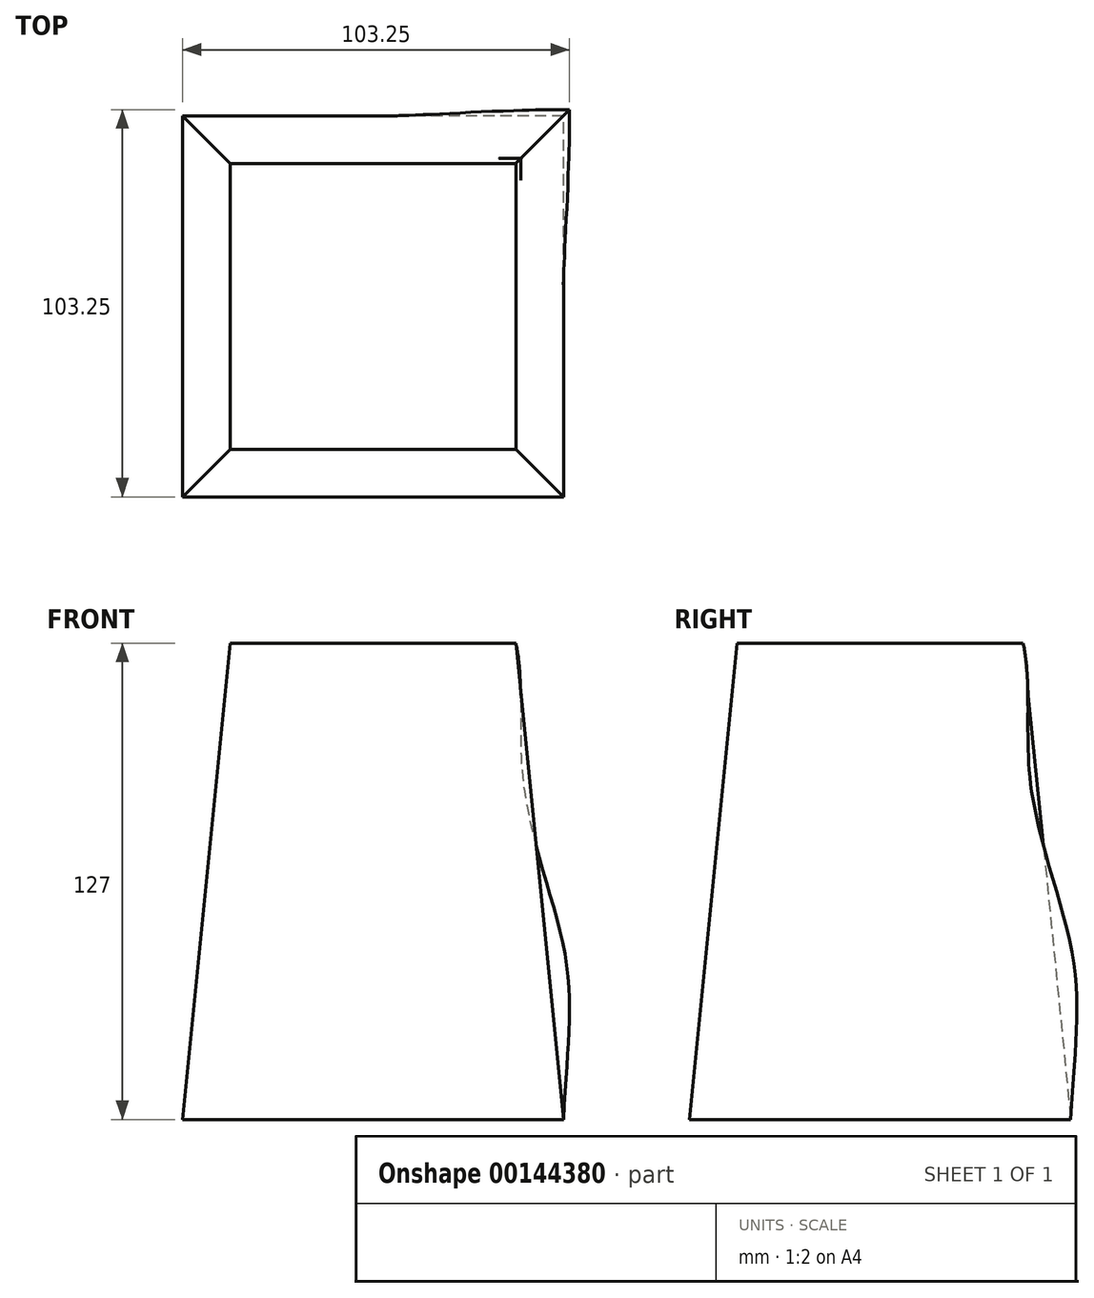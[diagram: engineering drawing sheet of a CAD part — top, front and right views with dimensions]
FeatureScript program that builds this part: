
annotation { "Feature Type Name" : "Feature", "Feature Type Description" : "" }
export const myFeature = defineFeature(function(context is Context, id is Id, definition is map)
    precondition{}
    {
        {
            var Q0;
            Q0=qCreatedBy(makeId("Top.planeOp"),FACE);
            var sketch = newSketch(context, id + "F0", { "sketchPlane" : qUnion([Q0])});
            skLineSegment(sketch, "E0.bottom", {"start": v(50.8, -50.8) * mm, "end": v(-50.8, -50.8) * mm});
            skLineSegment(sketch, "E0.top", {"start": v(50.8, 50.8) * mm, "end": v(-50.8, 50.8) * mm});
            skLineSegment(sketch, "E0.left", {"start": v(50.8, -50.8) * mm, "end": v(50.8, 50.8) * mm});
            skLineSegment(sketch, "E0.right", {"start": v(-50.8, -50.8) * mm, "end": v(-50.8, 50.8) * mm});
            skPoint(sketch, "E0.middle", {"position": v(0, 0) * mm});
            skSolve(sketch);
        }
        {
            var Q0;
            Q0=qCreatedBy(makeId("Top.planeOp"),FACE);
            cPlane(context, id + "F1", {"entities" : qUnion([Q0]), "cplaneType" : CPlaneType.OFFSET, "offset" : 127 * mm, "width" : 152.4 * mm, "height" : 152.4 * mm});
        }
        {
            var Q0;
            Q0=qCreatedBy(id+"F1.planeOp",FACE);
            var sketch = newSketch(context, id + "F2", { "sketchPlane" : qUnion([Q0])});
            skLineSegment(sketch, "E1.bottom", {"start": v(38.1, 38.1) * mm, "end": v(-38.1, 38.1) * mm});
            skLineSegment(sketch, "E1.top", {"start": v(38.1, -38.1) * mm, "end": v(-38.1, -38.1) * mm});
            skLineSegment(sketch, "E1.left", {"start": v(38.1, 38.1) * mm, "end": v(38.1, -38.1) * mm});
            skLineSegment(sketch, "E1.right", {"start": v(-38.1, 38.1) * mm, "end": v(-38.1, -38.1) * mm});
            skPoint(sketch, "E1.middle", {"position": v(0, 0) * mm});
            skSolve(sketch);
        }
        {
            var Q0;
            Q0=sQuery(id+"F2.wireOp",VERTEX,"E1.bottom.start");
            var Q1;
            Q1=sQuery(id+"F2.wireOp",VERTEX,"E1.right.end");
            var Q2;
            Q2=sQuery(id+"F0.wireOp",VERTEX,"E0.right.start");
            cPlane(context, id + "F3", {"entities" : qUnion([Q0, Q1, Q2]), "cplaneType" : CPlaneType.THREE_POINT, "offset" : 25.4 * mm, "width" : 152.4 * mm, "height" : 152.4 * mm});
        }
        {
            var Q0;
            Q0=qCreatedBy(id+"F3.planeOp",FACE);
            var sketch = newSketch(context, id + "F4", { "sketchPlane" : qUnion([Q0])});
            skFitSpline(sketch, "E2", {"points": [v(-53.88, 127) * mm, v(-56.82, 89.06) * mm, v(-72.9, 41.99) * mm, v(-71.84, 0) * mm], "startDerivative": vector(-32.58, -103.67) * mm, "endDerivative": vector(10.34, -156.62) * mm});
            skSolve(sketch);
        }
        {
            var Q0;
            Q0=qCreatedBy(makeId("Front.planeOp"),FACE);
            var sketch = newSketch(context, id + "F5", { "sketchPlane" : qUnion([Q0])});
            skLineSegment(sketch, "E3", {"start": v(0, 0) * mm, "end": v(0, 85.5) * mm});
            skSolve(sketch);
        }
        {
            var Q0;
            Q0=makeQuery(id+"F2.imprint","IMPRINT",FACE,{"disambiguationData":[TD([[makeQuery(id+"F2.imprint","IMPRINT",EDGE,{"derivedFrom":sQuery(id+"F2.wireOp",EDGE,"E1.bottom")}),1.0]])]});
            var Q1;
            Q1=makeQuery(id+"F0.imprint","IMPRINT",FACE,{"disambiguationData":[TD([[makeQuery(id+"F0.imprint","IMPRINT",EDGE,{"derivedFrom":sQuery(id+"F0.wireOp",EDGE,"E0.bottom")}),-1.0]])]});
            var Q2;
            Q2=sQuery(id+"F4.wireOp",EDGE,"E2");
            var Q3;
            Q3=sQuery(id+"Fryh11T3wm06IZR_0.2.F4.wireOp",EDGE,"E2");
            var Q4;
            Q4=sQuery(id+"Fryh11T3wm06IZR_0.1.F4.wireOp",EDGE,"E2");
            var Q5;
            Q5=sQuery(id+"Fryh11T3wm06IZR_0.3.F4.wireOp",EDGE,"E2");
            loft(context, id + "F6", {"addGuides" : true, "sheetProfilesArray" : [{ "sheetProfileEntities" : qUnion([Q0]) }, { "sheetProfileEntities" : qUnion([Q1]) }], "guidesArray" : [{ "guideEntities" : qUnion([Q2]), "guideDerivativeType" : LoftGuideDerivativeType.DEFAULT, "guideDerivativeMagnitude" : 1 }, { "guideEntities" : qUnion([Q3]), "guideDerivativeType" : LoftGuideDerivativeType.DEFAULT, "guideDerivativeMagnitude" : 1 }, { "guideEntities" : qUnion([Q4]), "guideDerivativeType" : LoftGuideDerivativeType.DEFAULT, "guideDerivativeMagnitude" : 1 }, { "guideEntities" : qUnion([Q5]), "guideDerivativeType" : LoftGuideDerivativeType.DEFAULT, "guideDerivativeMagnitude" : 1 }]});
        }
    });
